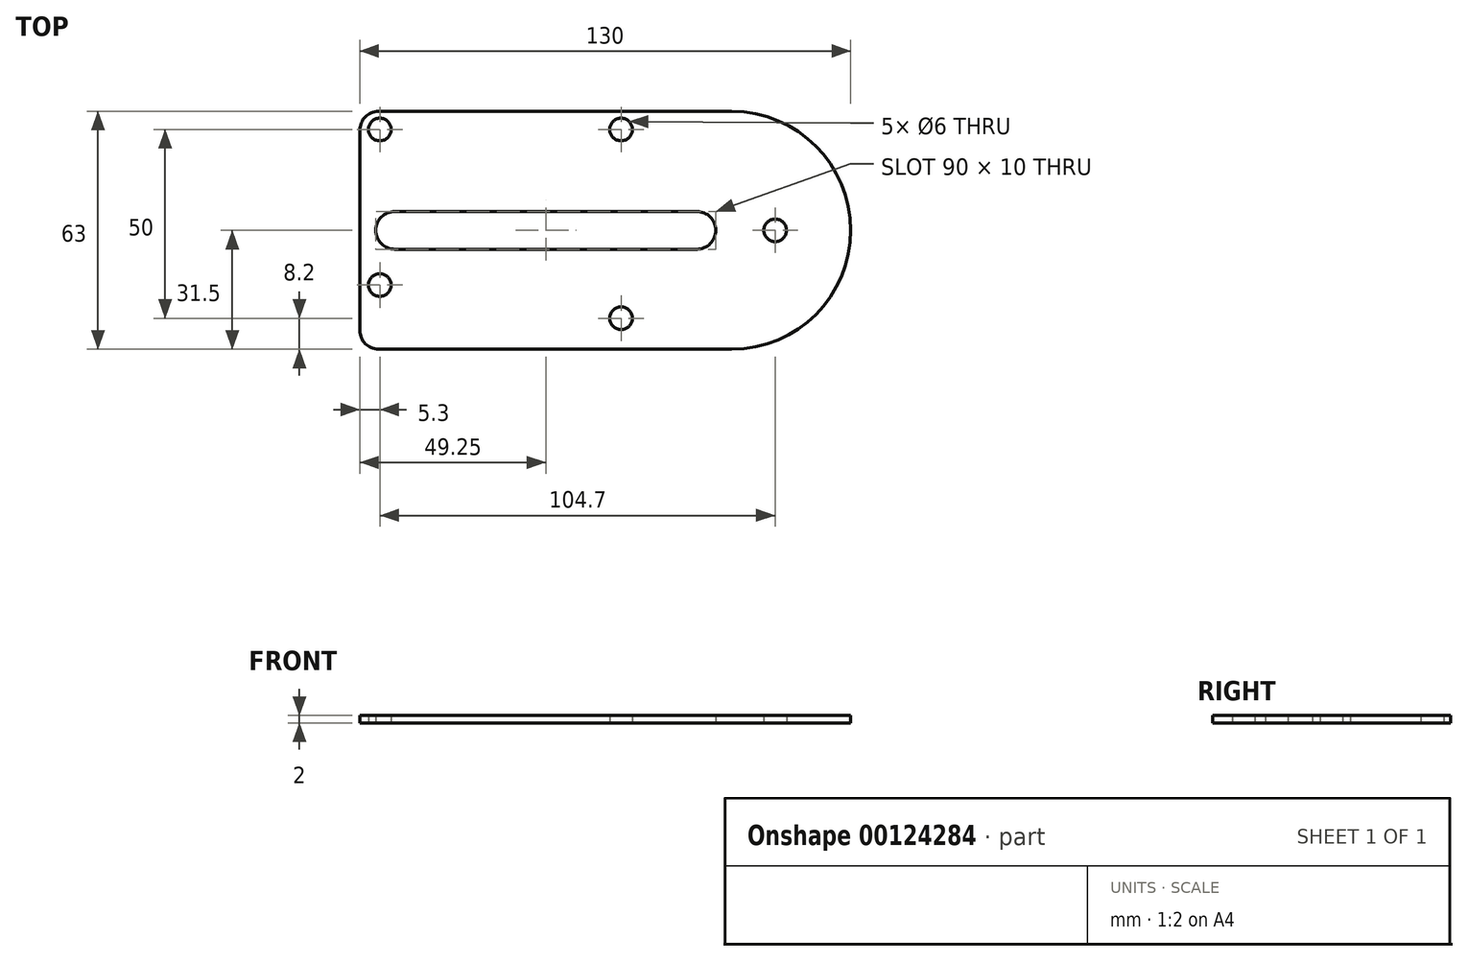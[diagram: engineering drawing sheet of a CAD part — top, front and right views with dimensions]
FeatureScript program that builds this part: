
annotation { "Feature Type Name" : "Feature", "Feature Type Description" : "" }
export const myFeature = defineFeature(function(context is Context, id is Id, definition is map)
    precondition{}
    {
        {
            var Q0;
            Q0=qCreatedBy(makeId("Top.planeOp"),FACE);
            var sketch = newSketch(context, id + "F0", { "sketchPlane" : qUnion([Q0])});
            skLineSegment(sketch, "E0.bottom", {"start": v(-98.5, 31.5) * mm, "end": v(0, 31.5) * mm});
            skLineSegment(sketch, "E0.top", {"start": v(-98.5, -31.5) * mm, "end": v(0, -31.5) * mm});
            skLineSegment(sketch, "E0.left", {"start": v(-98.5, 31.5) * mm, "end": v(-98.5, -31.5) * mm});
            skPoint(sketch, "E0.middle", {"position": v(0, 0) * mm});
            skPoint(sketch, "E1", {"position": v(-93.2, 26.7) * mm});
            skPoint(sketch, "E2", {"position": v(-29.3, 26.7) * mm});
            skPoint(sketch, "E3", {"position": v(-29.3, -23.3) * mm});
            skPoint(sketch, "E4", {"position": v(-93.2, -14.5) * mm});
            skPoint(sketch, "E5", {"position": v(11.5, 0) * mm});
            skArc(sketch, "E6", {"start": v(0, -31.5) * mm, "mid": v(31.5, 0) * mm, "end": v(0, 31.5) * mm});
            skLineSegment(sketch, "E7", {"start": v(-89.25, 0) * mm, "end": v(-9.25, 0) * mm});
            skArc(sketch, "E8.0.startCap", {"start": v(-89.25, -5) * mm, "mid": v(-94.25, 0) * mm, "end": v(-89.25, 5) * mm});
            skArc(sketch, "E8.0.endCap", {"start": v(-9.25, 5) * mm, "mid": v(-4.25, 0) * mm, "end": v(-9.25, -5) * mm});
            skLineSegment(sketch, "E8.0.left", {"start": v(-89.25, 5) * mm, "end": v(-9.25, 5) * mm});
            skLineSegment(sketch, "E8.0.right", {"start": v(-89.25, -5) * mm, "end": v(-9.25, -5) * mm});
            skSolve(sketch);
        }
        {
            var Q0;
            Q0=makeQuery(id+"F0.imprint","IMPRINT",FACE,{"disambiguationData":[TD([[makeQuery(id+"F0.imprint","IMPRINT",EDGE,{"derivedFrom":sQuery(id+"F0.wireOp",EDGE,"E0.bottom")}),-1.0]])]});
            extrude(context, id + "F1", {"entities" : qUnion([Q0]), "depth" : 2 * mm});
        }
        {
            var Q0;
            Q0=sQuery(id+"F0.wireOp",VERTEX,"E1");
            var Q1;
            Q1=sQuery(id+"F0.wireOp",VERTEX,"E4");
            var Q2;
            Q2=sQuery(id+"F0.wireOp",VERTEX,"E2");
            var Q3;
            Q3=sQuery(id+"F0.wireOp",VERTEX,"E3");
            var Q4;
            Q4=sQuery(id+"F0.wireOp",VERTEX,"E5");
            var Q5;
            Q5=makeQuery(id+"F1.opExtrude","SWEPT_BODY",BODY,{"disambiguationData":[OSD([sQuery(id+"F0.wireOp",EDGE,"E0.bottom"),sQuery(id+"F0.wireOp",EDGE,"E0.top"),sQuery(id+"F0.wireOp",EDGE,"E0.left"),sQuery(id+"F0.wireOp",EDGE,"E0.right")])]});
            hole(context, id + "F2", {"style" : HoleStyle.SIMPLE, "endStyle" : HoleEndStyle.THROUGH, "oppositeDirection" : true, "holeDiameter" : 6 * mm, "locations" : qUnion([Q0, Q1, Q2, Q3, Q4]), "scope" : qUnion([Q5]), "isTappedThrough" : true});
        }
        {
            var Q0;
            Q0=makeQuery(id+"F1.opExtrude","SWEPT_EDGE",EDGE,{"disambiguationData":[OSD([sQuery(id+"F0.wireOp",EDGE,"E0.bottom"),sQuery(id+"F0.wireOp",EDGE,"E0.left")])]});
            var Q1;
            Q1=makeQuery(id+"F1.opExtrude","SWEPT_EDGE",EDGE,{"disambiguationData":[OSD([sQuery(id+"F0.wireOp",EDGE,"E0.top"),sQuery(id+"F0.wireOp",EDGE,"E0.left")])]});
            fillet(context, id + "F3", {"entities" : qUnion([Q0, Q1]), "radius" : 5 * mm, "tangentPropagation" : true, "allowEdgeOverflow" : false});
        }
    });
